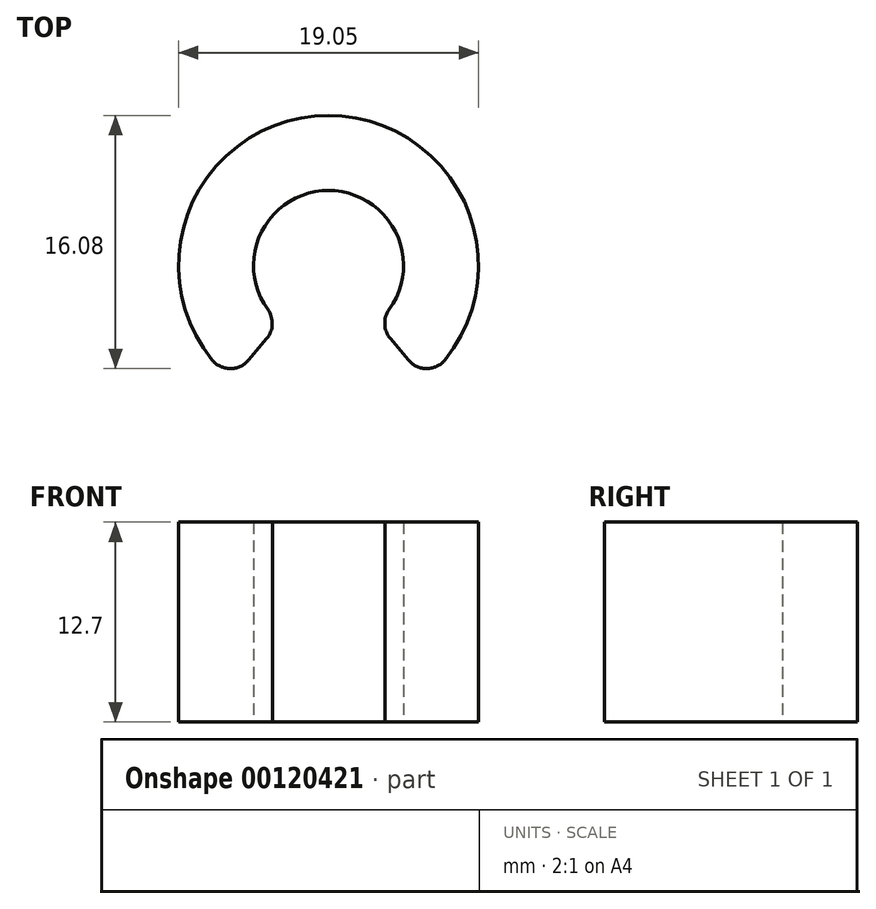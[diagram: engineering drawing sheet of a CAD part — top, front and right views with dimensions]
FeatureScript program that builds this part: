
annotation { "Feature Type Name" : "Feature", "Feature Type Description" : "" }
export const myFeature = defineFeature(function(context is Context, id is Id, definition is map)
    precondition{}
    {
        {
            var Q0;
            Q0=qCreatedBy(makeId("Top.planeOp"),FACE);
            var sketch = newSketch(context, id + "F0", { "sketchPlane" : qUnion([Q0])});
            skArc(sketch, "E0", {"start": v(-19.6, -6) * mm, "mid": v(-27, 9.53) * mm, "end": v(-34.4, -6) * mm});
            skArc(sketch, "E1", {"start": v(-6.78, -5.5) * mm, "mid": v(0, 8.73) * mm, "end": v(6.78, -5.5) * mm});
            skArc(sketch, "E2.0", {"start": v(-3.25, -2.28) * mm, "mid": v(0, 3.97) * mm, "end": v(3.25, -2.28) * mm});
            skArc(sketch, "E3.0", {"start": v(-23.14, -2.8) * mm, "mid": v(-27, 4.76) * mm, "end": v(-30.85, -2.8) * mm});
            skLineSegment(sketch, "E4", {"start": v(-23.07, -4.64) * mm, "end": v(-21.9, -6.02) * mm});
            skLineSegment(sketch, "E5", {"start": v(-30.92, -4.64) * mm, "end": v(-32.09, -6.02) * mm});
            skPoint(sketch, "E6.visualSharp", {"position": v(-30.07, -3.64) * mm});
            skArc(sketch, "E6.filletArc", {"start": v(-30.92, -4.64) * mm, "mid": v(-30.57, -3.73) * mm, "end": v(-30.85, -2.8) * mm});
            skPoint(sketch, "E7.visualSharp", {"position": v(-23.92, -3.64) * mm});
            skArc(sketch, "E7.filletArc", {"start": v(-23.14, -2.8) * mm, "mid": v(-23.42, -3.73) * mm, "end": v(-23.07, -4.64) * mm});
            skPoint(sketch, "E8.visualSharp", {"position": v(-33.15, -7.27) * mm});
            skArc(sketch, "E8.filletArc", {"start": v(-34.4, -6) * mm, "mid": v(-33.25, -6.55) * mm, "end": v(-32.09, -6.02) * mm});
            skPoint(sketch, "E9.visualSharp", {"position": v(-20.84, -7.27) * mm});
            skArc(sketch, "E9.filletArc", {"start": v(-21.9, -6.02) * mm, "mid": v(-20.74, -6.55) * mm, "end": v(-19.6, -6) * mm});
            skLineSegment(sketch, "E10", {"start": v(-4.45, -5.5) * mm, "end": v(-3.31, -4.09) * mm});
            skLineSegment(sketch, "E11", {"start": v(3.31, -4.09) * mm, "end": v(4.45, -5.5) * mm});
            skPoint(sketch, "E12.visualSharp", {"position": v(-5.5, -6.78) * mm});
            skArc(sketch, "E12.filletArc", {"start": v(-6.78, -5.5) * mm, "mid": v(-5.62, -6.05) * mm, "end": v(-4.45, -5.5) * mm});
            skPoint(sketch, "E13.visualSharp", {"position": v(-2.5, -3.08) * mm});
            skArc(sketch, "E13.filletArc", {"start": v(-3.31, -4.09) * mm, "mid": v(-2.98, -3.2) * mm, "end": v(-3.25, -2.28) * mm});
            skPoint(sketch, "E14.visualSharp", {"position": v(2.5, -3.08) * mm});
            skArc(sketch, "E14.filletArc", {"start": v(3.25, -2.28) * mm, "mid": v(2.98, -3.2) * mm, "end": v(3.31, -4.09) * mm});
            skPoint(sketch, "E15.visualSharp", {"position": v(5.5, -6.78) * mm});
            skArc(sketch, "E15.filletArc", {"start": v(4.45, -5.5) * mm, "mid": v(5.62, -6.05) * mm, "end": v(6.78, -5.5) * mm});
            skLineSegment(sketch, "E16", {"start": v(-27, 0) * mm, "end": v(-27, 4.76) * mm, "construction": true});
            skLineSegment(sketch, "E17", {"start": v(-30.07, -3.64) * mm, "end": v(-27, 0) * mm, "construction": true});
            skLineSegment(sketch, "E18", {"start": v(-3.97, 0) * mm, "end": v(3.97, 0) * mm, "construction": true});
            skLineSegment(sketch, "E19", {"start": v(-31.76, 0) * mm, "end": v(-22.23, 0) * mm, "construction": true});
            skLineSegment(sketch, "E20", {"start": v(-35.84, 2.45) * mm, "end": v(-37.88, 3.68) * mm, "construction": true});
            skLineSegment(sketch, "E21", {"start": v(-37.88, 3.68) * mm, "end": v(-39.93, 4.9) * mm, "construction": true});
            skLineSegment(sketch, "E22", {"start": v(-37.88, 3.68) * mm, "end": v(-31.76, 0) * mm, "construction": true});
            skLineSegment(sketch, "E23", {"start": v(-30.57, -3.67) * mm, "end": v(-23.42, -3.67) * mm, "construction": true});
            skLineSegment(sketch, "E24", {"start": v(-23.42, -3.67) * mm, "end": v(-23.42, -7.1) * mm, "construction": true});
            skLineSegment(sketch, "E25", {"start": v(-35.84, 2.45) * mm, "end": v(-33.8, 1.23) * mm, "construction": true});
            skLineSegment(sketch, "E26", {"start": v(-33.8, 1.23) * mm, "end": v(-31.76, 0) * mm, "construction": true});
            skLineSegment(sketch, "E27", {"start": v(-31.76, 0) * mm, "end": v(-39.93, 4.9) * mm, "construction": true});
            skLineSegment(sketch, "E28", {"start": v(2.98, -8.46) * mm, "end": v(2.98, -3.14) * mm, "construction": true});
            skLineSegment(sketch, "E29", {"start": v(2.98, -3.14) * mm, "end": v(-2.98, -3.14) * mm, "construction": true});
            skLineSegment(sketch, "E30", {"start": v(-2.98, -3.14) * mm, "end": v(-4.29, -1.65) * mm, "construction": true});
            skLineSegment(sketch, "E31", {"start": v(-4.29, -1.65) * mm, "end": v(-5.6, -0.16) * mm, "construction": true});
            skLineSegment(sketch, "E32", {"start": v(-5.6, -0.16) * mm, "end": v(-6.9, 1.33) * mm, "construction": true});
            skLineSegment(sketch, "E33", {"start": v(-6.9, 1.33) * mm, "end": v(-8.22, 2.82) * mm, "construction": true});
            skLineSegment(sketch, "E34", {"start": v(-6.9, 1.33) * mm, "end": v(-2.98, -3.14) * mm, "construction": true});
            skLineSegment(sketch, "E35", {"start": v(-2.98, -3.14) * mm, "end": v(-8.22, 2.82) * mm, "construction": true});
            skLineSegment(sketch, "E36", {"start": v(-2.98, -3.14) * mm, "end": v(-2.98, -7.4) * mm, "construction": true});
            skSolve(sketch);
        }
        {
            var Q0;
            Q0=makeQuery(id+"F0.imprint","IMPRINT",FACE,{"disambiguationData":[TD([[makeQuery(id+"F0.imprint","IMPRINT",EDGE,{"derivedFrom":sQuery(id+"F0.wireOp",EDGE,"E0")}),1.0]])]});
            var Q1;
            Q1=makeQuery(id+"F0.imprint","IMPRINT",FACE,{"disambiguationData":[TD([[makeQuery(id+"F0.imprint","IMPRINT",EDGE,{"derivedFrom":sQuery(id+"F0.wireOp",EDGE,"E1")}),-1.0]])]});
            extrude(context, id + "F1", {"entities" : qUnion([Q0, Q1]), "depth" : 12.7 * mm});
        }
    });
